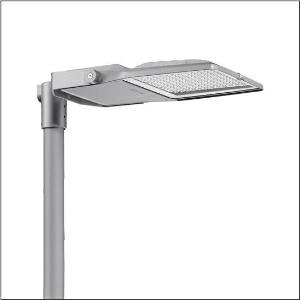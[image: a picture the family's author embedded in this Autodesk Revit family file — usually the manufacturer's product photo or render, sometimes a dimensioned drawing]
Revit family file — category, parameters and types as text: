
# Revit family: floodlight_fl_21_iq_midi___pl33t_5xa7782f2f3a_348f
name_source: partatom
category: Lighting Fixtures
units: mm (PartAtom-declared; Revit-internal decimal feet)

## family parameters
Cut with Voids When Loaded = No
Host = Face
Light Source = No
Part Type = Normal
Room Calculation Point = No
Round Connector Dimension = Use Diameter
Shared = No

## types (1)
- --- (1 x LED, 35350 lm, 270.2 W, 3000K)
    Apparent Load = 270 VA
    CIE Flux Codes = 26 75 99 100 100
    Color Rendering = 70
    Color Temperature = 3000K
    Default Elevation = 1800 mm
    Description = Floodlight FL 21 iQ midi, floodlight, primary light control with lens, of PMMA, primary optical cover: protective disc, of toughened safety glass, transparent, light distribution: PL33T, light emission: direct distribution, installation type: surface-mounted, LED, High Power LED, rated luminous flux: 35.350lm, luminous efficacy: 131lm/W, light colour: 730, colour temperature: 3000K, control gear: ECG iQ, control: optimised constant luminous flux control (CLO 2.0), Desk-Remote (wireless, voltage-free reading and setting of iQ features in the workshop via application-optimized NFC function/RFID function), Smart-Wire, Night-Set, Temp-Guard, Auto-Match, Street-Remote, with terminal, 6-pole, mains connection: 220..240V, AC, 50/60Hz, start of lifetime: 270W, end of service life: 287W, reduction: 117W, luminaire housing, of diecast aluminium, powder-coated, Siteco® metallic grey (DB 702S), corrosivity category C5 mid according to DIN EN ISO 12944, sealing non-destructively replaceable, please order mast flange separately, mast bracket, of steel, galvanised, powder-coated, Siteco® metallic grey (DB 702S), protection rating (complete): IP66, insulation class (complete): insulation class II (safety insulation), certification: CE, ENEC, VDE, protection symbol: D, impact resistance: IK08, permissible operating ambient temperature: -40..+40°C, permissible operating ambient temperature for outdoor applications: -40..+50°C, standard: DIN EN 12944, LABS conformity tested according to VDMA 24364:2018-05, packaging unit: 1 piece

Light Distribution: PL33T
    Height = 76 mm
    Lamp = 1 x LED
    Lamp Light Flux = 35350 lm
    Lamp Power = 270.2 W
    Lamp count = 1
    Length = 657 mm
    Luminous efficacy = 131 lm/W
    Manufacturer = Siteco
    ModVariant = No
    Model = 5XA7782F2F3A
    Number of Poles = 1
    OnlyDefault = Yes
    Power Factor = 1
    Product Name = Floodlight FL 21 iQ midi | PL33T
    Product group = floodlight | pylon annexe
    ProductGroupID = 6200
    Protection Class = Protection class II
    Protection Degree = IP 66
    RLX_Detail_Level = 1
    RLX_Emergency_Light_Flux = 0 lm
    RLX_Emergency_Type = 0
    RLX_Emergency_Type_DB = No
    RlxData = <blob elided: 153569 chars, md5=175e69a6>
    Socket = socket
    Standby Power = 0 W
    System Light Flux = 35350 lm
    System Power = 270 W
    Type Comments = factory setting: luminous flux: 100 % | dim-lin: 254 | 620 mA
    Type Image = l_1007123.jpg
    URL = http://relux.com
    VarID = @adj_072221
    Voltage = 0 V
    Weight = 0.00 kg
    Width = 442 mm

## geometry (parser evidence)
native form markers: Blend x4, Sweep x14
no freeform markers — native parametric forms only
